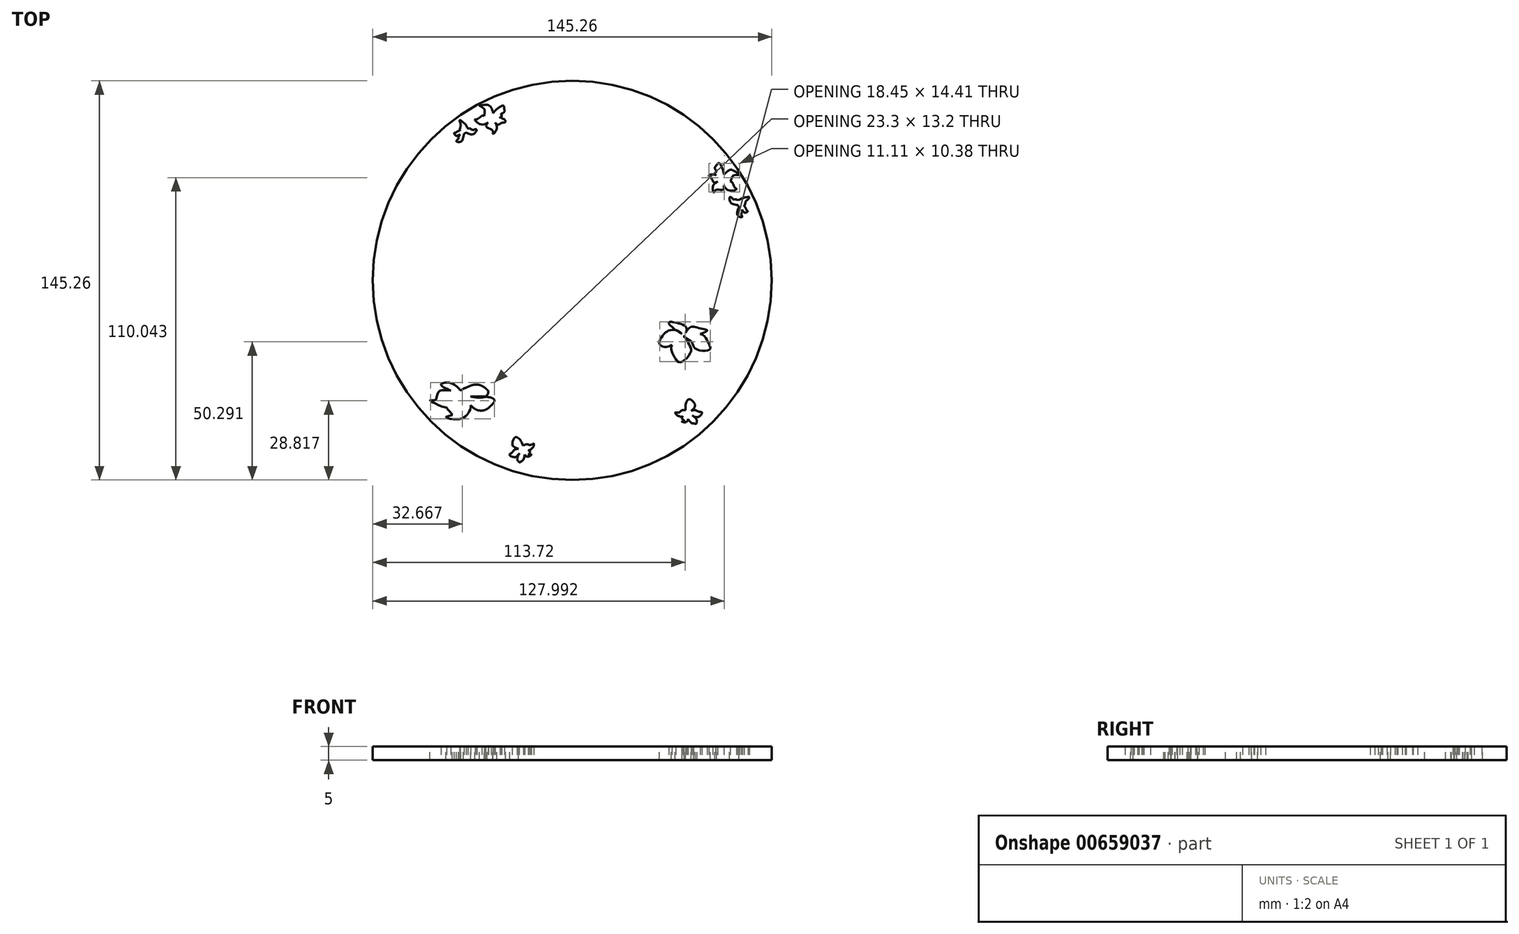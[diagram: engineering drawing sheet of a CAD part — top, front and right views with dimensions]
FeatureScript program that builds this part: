
annotation { "Feature Type Name" : "Feature", "Feature Type Description" : "" }
export const myFeature = defineFeature(function(context is Context, id is Id, definition is map)
    precondition{}
    {
        {
            var Q0;
            Q0=qCreatedBy(makeId("Top.planeOp"),FACE);
            var sketch = newSketch(context, id + "F0", { "sketchPlane" : qUnion([Q0])});
            skCircle(sketch, "E0", {"center": v(0, 0) * mm, "radius": 74.63 * mm});
            skFitSpline(sketch, "E1", {"points": [v(-40.91, 58.34) * mm, v(-40.6, 56.7) * mm, v(-40.85, 55.34) * mm, v(-40.76, 53.16) * mm, v(-39.4, 53.35) * mm, v(-38.04, 55.3) * mm, v(-40.91, 58.34) * mm]});
            skFitSpline(sketch, "E2", {"points": [v(-38.04, 55.3) * mm, v(-37.18, 55.3) * mm, v(-36.22, 54.76) * mm, v(-35.4, 55.04) * mm, v(-34.76, 54.83) * mm, v(-35.4, 53.73) * mm, v(-36.63, 53.12) * mm, v(-38.68, 53.8) * mm], "startDerivative": vector(6.82, 1.47) * mm, "endDerivative": vector(-10.95, 4.9) * mm});
            skFitSpline(sketch, "E3", {"points": [v(-40.98, 54.45) * mm, v(-41.87, 54.19) * mm, v(-42.51, 53.68) * mm, v(-42.97, 53.73) * mm, v(-42.43, 52.71) * mm, v(-40.76, 53.16) * mm], "startDerivative": vector(-4.99, 0.27) * mm, "endDerivative": vector(6.89, 3.52) * mm});
            skFitSpline(sketch, "E4", {"points": [v(-40.76, 53.16) * mm, v(-41.37, 52.23) * mm, v(-41.37, 51.64) * mm, v(-42, 51.05) * mm, v(-42.16, 50.65) * mm, v(-41.37, 50.38) * mm, v(-40.18, 50.75) * mm, v(-39.4, 53.35) * mm], "startDerivative": vector(-5.91, -5.6) * mm, "endDerivative": vector(2.42, 13) * mm});
            skFitSpline(sketch, "E5", {"points": [v(-39.6, 52.34) * mm, v(-39.4, 51.05) * mm, v(-38.76, 50.73) * mm, v(-38.22, 50) * mm, v(-38.49, 49.87) * mm, v(-38.09, 49.74) * mm, v(-37.4, 50.51) * mm, v(-37.36, 51.43) * mm, v(-37.42, 52.34) * mm, v(-37.96, 53.48) * mm], "startDerivative": vector(-0.1, -10.73) * mm, "endDerivative": vector(-5.2, 8.29) * mm});
            skFitSpline(sketch, "E6", {"points": [v(-33.8, 63.65) * mm, v(-31.96, 62.26) * mm, v(-32, 59.88) * mm, v(-30.3, 58.89) * mm, v(-28.92, 60.06) * mm, v(-29.1, 62.04) * mm, v(-30.24, 63.73) * mm, v(-32.5, 63.84) * mm, v(-33.8, 63.65) * mm]});
            skFitSpline(sketch, "E7", {"points": [v(-28.82, 60.86) * mm, v(-27.82, 61.97) * mm, v(-25.8, 63.47) * mm, v(-25.07, 63.62) * mm, v(-24.81, 62.92) * mm, v(-24.81, 61.2) * mm, v(-25.91, 60.54) * mm, v(-25.62, 59.77) * mm, v(-27.41, 59.13) * mm, v(-28.92, 60.06) * mm], "startDerivative": vector(7.39, 9) * mm, "endDerivative": vector(-9.5, 11.77) * mm});
            skFitSpline(sketch, "E8", {"points": [v(-32, 59.88) * mm, v(-32.91, 59.88) * mm, v(-34.76, 58.63) * mm, v(-35.4, 58.6) * mm, v(-33.94, 57.02) * mm, v(-30.68, 57.48) * mm, v(-29.61, 59.13) * mm, v(-29.64, 59.13) * mm], "startDerivative": vector(-7.49, 2.17) * mm, "endDerivative": vector(-5.62, -1.67) * mm});
            skFitSpline(sketch, "E9", {"points": [v(-30.68, 57.48) * mm, v(-31.26, 55.98) * mm, v(-28.92, 54.45) * mm, v(-28.92, 53.48) * mm, v(-28.3, 53.73) * mm, v(-27.41, 56.01) * mm, v(-29.61, 59.13) * mm], "startDerivative": vector(-8.57, -10.2) * mm, "endDerivative": vector(-13.08, 12.83) * mm});
            skFitSpline(sketch, "E10", {"points": [v(-28.08, 57.48) * mm, v(-27.05, 56.65) * mm, v(-25.4, 57.48) * mm, v(-24.6, 57.48) * mm, v(-24.26, 58.12) * mm, v(-26.22, 59.3) * mm, v(-26.33, 59.26) * mm], "startDerivative": vector(4.67, -5.14) * mm, "endDerivative": vector(-1.23, -1.34) * mm});
            skFitSpline(sketch, "E11", {"points": [v(40.7, -20.4) * mm, v(36.32, -23.45) * mm, v(36.83, -27.11) * mm, v(39.27, -29.76) * mm, v(43.24, -25.8) * mm, v(42.42, -23.05) * mm, v(40.7, -20.4) * mm]});
            skFitSpline(sketch, "E12", {"points": [v(40.7, -20.4) * mm, v(43.34, -22.23) * mm, v(44.76, -24.78) * mm, v(50.05, -25.18) * mm, v(49.64, -22.74) * mm, v(46.6, -19.49) * mm, v(40.7, -20.4) * mm]});
            skFitSpline(sketch, "E13", {"points": [v(40.7, -20.4) * mm, v(38.11, -18.16) * mm, v(34.68, -18.49) * mm, v(32.72, -20.4) * mm, v(31.82, -23.06) * mm, v(34.02, -24.2) * mm, v(36.32, -23.45) * mm], "startDerivative": vector(-12.48, 15.48) * mm, "endDerivative": vector(13.93, 7.55) * mm});
            skFitSpline(sketch, "E14", {"points": [v(39.94, -19.46) * mm, v(36.32, -16.93) * mm, v(35.17, -15.3) * mm, v(38.11, -15.46) * mm, v(41.62, -17.26) * mm, v(40.7, -20.4) * mm], "startDerivative": vector(-16.5, 10.24) * mm, "endDerivative": vector(-8.67, -17.52) * mm});
            skFitSpline(sketch, "E15", {"points": [v(41.27, -19.23) * mm, v(43.18, -16.93) * mm, v(46.7, -17.5) * mm, v(49.14, -18.16) * mm, v(46.6, -19.49) * mm], "startDerivative": vector(6.21, 12.18) * mm, "endDerivative": vector(-15.88, -6.24) * mm});
            skFitSpline(sketch, "E16", {"points": [v(-40.74, -40.65) * mm, v(-44.04, -42.43) * mm, v(-45.7, -46.36) * mm, v(-43.79, -48.9) * mm, v(-45.95, -49.66) * mm, v(-42.01, -50.55) * mm, v(-38.08, -48.65) * mm, v(-36.9, -45.47) * mm, v(-37.95, -42.3) * mm, v(-40.74, -40.65) * mm]});
            skFitSpline(sketch, "E17", {"points": [v(-36.9, -45.47) * mm, v(-32.84, -47.38) * mm, v(-29.41, -45.47) * mm, v(-28.4, -43.44) * mm, v(-31.7, -42.3) * mm, v(-36.9, -42.3) * mm], "startDerivative": vector(18.8, -13.39) * mm, "endDerivative": vector(-21.47, 0.17) * mm});
            skFitSpline(sketch, "E18", {"points": [v(-40.74, -40.65) * mm, v(-48.74, -40.65) * mm, v(-49.88, -43.57) * mm, v(-51.78, -43.57) * mm, v(-48.48, -45.47) * mm, v(-45.7, -46.36) * mm], "startDerivative": vector(-35.6, 5.67) * mm, "endDerivative": vector(13.06, -2.8) * mm});
            skFitSpline(sketch, "E19", {"points": [v(-44.22, -40.1) * mm, v(-47.72, -37.86) * mm, v(-44.22, -37.35) * mm, v(-40.74, -40.1) * mm, v(-40.74, -40.65) * mm], "startDerivative": vector(-18.42, 7.74) * mm, "endDerivative": vector(-1.16, -4.68) * mm});
            skFitSpline(sketch, "E20", {"points": [v(-40.7, -40.48) * mm, v(-34.68, -37.9) * mm, v(-31.45, -39.36) * mm, v(-30.56, -40.65) * mm, v(-35.22, -42.32) * mm], "startDerivative": vector(19.8, 12.05) * mm, "endDerivative": vector(-23.97, -4.7) * mm});
            skFitSpline(sketch, "E21", {"points": [v(42.46, -43.24) * mm, v(41.27, -45.47) * mm, v(41.27, -47.24) * mm, v(41.27, -48.54) * mm, v(44.44, -46.36) * mm, v(44.39, -44.5) * mm, v(42.46, -43.24) * mm]});
            skFitSpline(sketch, "E22", {"points": [v(41.27, -47.24) * mm, v(39.94, -47.24) * mm, v(39.3, -47.81) * mm, v(38.11, -48.15) * mm, v(37.52, -48.1) * mm, v(38.11, -49.07) * mm, v(39.07, -49.47) * mm, v(39.94, -49.58) * mm, v(41.27, -48.54) * mm], "startDerivative": vector(-11.28, 1.59) * mm, "endDerivative": vector(9.13, 8.93) * mm});
            skFitSpline(sketch, "E23", {"points": [v(40.35, -49.38) * mm, v(39.94, -50.13) * mm, v(40.18, -50.52) * mm, v(40.8, -51.05) * mm, v(40.27, -51.26) * mm, v(39.94, -51.4) * mm, v(40.8, -51.63) * mm, v(41.57, -51.48) * mm, v(42.05, -50.96) * mm, v(42.15, -50.35) * mm, v(42.16, -49.77) * mm, v(42.1, -49.3) * mm, v(41.85, -49) * mm, v(41.27, -48.54) * mm], "startDerivative": vector(-6.6, -9.03) * mm, "endDerivative": vector(-6.76, 6.2) * mm});
            skFitSpline(sketch, "E24", {"points": [v(42.15, -50.35) * mm, v(42.66, -51.1) * mm, v(43.68, -52.02) * mm, v(44.58, -52.1) * mm, v(45.02, -52.24) * mm, v(45.24, -51.81) * mm, v(45.4, -50.92) * mm, v(44.83, -50) * mm, v(43.81, -49.2) * mm, v(42.65, -49) * mm, v(41.46, -48.71) * mm], "startDerivative": vector(4.58, -7.2) * mm, "endDerivative": vector(-10.04, 3.34) * mm});
            skFitSpline(sketch, "E25", {"points": [v(43.32, -47.5) * mm, v(45, -47.24) * mm, v(45.9, -47.71) * mm, v(46.82, -47.86) * mm, v(47.23, -48.15) * mm, v(46.99, -48.85) * mm, v(46.37, -49.4) * mm, v(45.56, -49.76) * mm, v(44.22, -49.43) * mm, v(43.81, -49.2) * mm], "startDerivative": vector(12.1, 3.78) * mm, "endDerivative": vector(-3.9, 2.83) * mm});
            skCircle(sketch, "E26.0", {"center": v(0, 0) * mm, "radius": 72.63 * mm});
            skFitSpline(sketch, "E27.MirrorCS", {"points": [v(61.79, 25.88) * mm, v(61.85, 24.77) * mm, v(61.56, 24.26) * mm, v(61.82, 23.43) * mm, v(61.76, 23) * mm, v(60.93, 23.16) * mm, v(60.09, 24.08) * mm, v(60.7, 26.71) * mm], "startDerivative": vector(2.34, -7.8) * mm, "endDerivative": vector(4.22, 11.8) * mm});
            skFitSpline(sketch, "E28.MirrorCS", {"points": [v(62.62, 26.88) * mm, v(63.26, 26.22) * mm, v(63.57, 25.46) * mm, v(63.99, 25.28) * mm, v(63.02, 24.66) * mm, v(61.79, 25.88) * mm], "startDerivative": vector(4.46, -2.24) * mm, "endDerivative": vector(-4.23, 6.47) * mm});
            skFitSpline(sketch, "E29.MirrorCS", {"points": [v(60.38, 25.8) * mm, v(59.56, 24.72) * mm, v(58.84, 24.76) * mm, v(58.02, 24.4) * mm, v(58.18, 24.15) * mm, v(57.77, 24.23) * mm, v(57.55, 25.26) * mm, v(57.98, 26.06) * mm, v(58.48, 26.83) * mm, v(59.55, 27.55) * mm], "startDerivative": vector(-5.25, -9.36) * mm, "endDerivative": vector(8.63, 4.6) * mm});
            skFitSpline(sketch, "E30.MirrorCS", {"points": [v(52.93, 35.92) * mm, v(51.62, 35.72) * mm, v(50.6, 37.26) * mm, v(49.9, 37.66) * mm, v(49.93, 38.38) * mm, v(52.21, 38.43) * mm, v(52.3, 38.34) * mm], "startDerivative": vector(-6.6, -2.14) * mm, "endDerivative": vector(0.8, -0.88) * mm});
            skFitSpline(sketch, "E31.MirrorC", {"points": [v(64.5, 30.3) * mm, v(63.42, 29.03) * mm, v(62.95, 27.73) * mm, v(61.79, 25.88) * mm, v(60.7, 26.71) * mm, v(60.5, 29.08) * mm, v(64.5, 30.3) * mm]});
            skFitSpline(sketch, "E32.MirrorCS", {"points": [v(60.5, 29.08) * mm, v(59.74, 29.5) * mm, v(58.64, 29.53) * mm, v(58.06, 30.17) * mm, v(57.41, 30.3) * mm, v(57.42, 29.04) * mm, v(58.18, 27.9) * mm, v(60.3, 27.47) * mm], "startDerivative": vector(-5.19, 4.66) * mm, "endDerivative": vector(11.46, -1.13) * mm});
            skFitSpline(sketch, "E33.MirrorCS", {"points": [v(55.26, 38.5) * mm, v(54.93, 39.95) * mm, v(53.93, 42.26) * mm, v(53.37, 42.75) * mm, v(52.8, 42.27) * mm, v(51.94, 40.78) * mm, v(52.57, 39.66) * mm, v(51.93, 39.14) * mm, v(53.17, 37.69) * mm, v(54.94, 37.75) * mm], "startDerivative": vector(-1.94, 11.48) * mm, "endDerivative": vector(14.08, 5.5) * mm});
            skFitSpline(sketch, "E34.MirrorCS", {"points": [v(57.52, 36.06) * mm, v(58.31, 35.6) * mm, v(59.3, 33.6) * mm, v(59.83, 33.26) * mm, v(57.78, 32.62) * mm, v(55.18, 34.64) * mm, v(55.08, 36.6) * mm, v(55.1, 36.58) * mm], "startDerivative": vector(7.58, -1.84) * mm, "endDerivative": vector(4.05, -4.25) * mm});
            skFitSpline(sketch, "E35.MirrorCS", {"points": [v(55.18, 34.64) * mm, v(54.94, 33.04) * mm, v(52.15, 32.88) * mm, v(51.66, 32.02) * mm, v(51.25, 32.57) * mm, v(51.62, 34.99) * mm, v(55.08, 36.6) * mm], "startDerivative": vector(2.36, -13.1) * mm, "endDerivative": vector(17.72, 4.63) * mm});
            skFitSpline(sketch, "E36.MirrorC", {"points": [v(60.95, 38.45) * mm, v(58.67, 38.15) * mm, v(57.52, 36.06) * mm, v(55.56, 36.04) * mm, v(54.94, 37.75) * mm, v(56.08, 39.38) * mm, v(57.9, 40.28) * mm, v(59.93, 39.24) * mm, v(60.95, 38.45) * mm]});
            skFitSpline(sketch, "E37.MirrorCS", {"points": [v(-16.04, -61.73) * mm, v(-15.35, -62.22) * mm, v(-15.4, -62.68) * mm, v(-15.8, -63.45) * mm, v(-15.18, -63.4) * mm, v(-14.82, -63.39) * mm, v(-15.55, -63.97) * mm, v(-16.27, -64.14) * mm, v(-16.93, -63.87) * mm, v(-17.27, -63.35) * mm, v(-17.52, -62.83) * mm, v(-17.67, -62.4) * mm, v(-17.56, -62) * mm, v(-17.28, -61.36) * mm], "startDerivative": vector(9.76, -5.45) * mm, "endDerivative": vector(3.55, 8.47) * mm});
            skFitSpline(sketch, "E38.MirrorCS", {"points": [v(-17.82, -60.18) * mm, v(-16.56, -59.6) * mm, v(-15.74, -59.85) * mm, v(-14.52, -59.67) * mm, v(-14, -59.37) * mm, v(-14.13, -60.5) * mm, v(-14.83, -61.26) * mm, v(-15.58, -61.73) * mm, v(-17.28, -61.36) * mm], "startDerivative": vector(9.58, 6.15) * mm, "endDerivative": vector(-12.03, 4.3) * mm});
            skFitSpline(sketch, "E39.MirrorCS", {"points": [v(-17.27, -63.35) * mm, v(-17.42, -64.26) * mm, v(-17.97, -65.5) * mm, v(-18.75, -65.95) * mm, v(-19.09, -66.27) * mm, v(-19.47, -65.97) * mm, v(-20, -65.23) * mm, v(-19.86, -64.15) * mm, v(-19.26, -63) * mm, v(-18.28, -62.34) * mm, v(-17.38, -61.6) * mm], "startDerivative": vector(-1.16, -8.45) * mm, "endDerivative": vector(7.72, 7.23) * mm});
            skFitSpline(sketch, "E40.MirrorCS", {"points": [v(-19.53, -61.26) * mm, v(-21.16, -61.72) * mm, v(-21.77, -62.52) * mm, v(-22.55, -63.04) * mm, v(-22.8, -63.48) * mm, v(-22.3, -64) * mm, v(-21.5, -64.26) * mm, v(-20.61, -64.24) * mm, v(-19.54, -63.38) * mm, v(-19.26, -63) * mm], "startDerivative": vector(-12.57, -1.61) * mm, "endDerivative": vector(2.36, 4.2) * mm});
            skFitSpline(sketch, "E41.MirrorC", {"points": [v(-20.52, -57.02) * mm, v(-18.56, -58.58) * mm, v(-17.82, -60.18) * mm, v(-17.28, -61.36) * mm, v(-21.02, -60.69) * mm, v(-21.75, -58.96) * mm, v(-20.52, -57.02) * mm]});
            skLineSegment(sketch, "E42", {"start": v(-35.22, -42.32) * mm, "end": v(-35.42, -42.28) * mm});
            skFitSpline(sketch, "E43", {"points": [v(-40.74, -40.1) * mm, v(-39.72, -39.47) * mm, v(-37.69, -38.62) * mm, v(-34.68, -37.9) * mm, v(-31.45, -39.36) * mm, v(-30.56, -40.65) * mm, v(-31.7, -42.3) * mm, v(-36.9, -42.3) * mm], "startDerivative": vector(9.53, 6.46) * mm, "endDerivative": vector(-29.55, 4.4) * mm});
            skFitSpline(sketch, "E44", {"points": [v(-36.9, -42.3) * mm, v(-34.89, -42.6) * mm, v(-32.2, -43.04) * mm, v(-28.4, -43.44) * mm, v(-29.41, -45.47) * mm, v(-32.84, -47.38) * mm, v(-35.54, -46.7) * mm, v(-36.9, -45.47) * mm], "startDerivative": vector(16.39, -1.98) * mm, "endDerivative": vector(-10.05, 11.08) * mm});
            skSolve(sketch);
        }
        {
            var Q0;
            Q0=makeQuery(id+"F0.imprint","IMPRINT",FACE,{"disambiguationData":[TD([[makeQuery(id+"F0.imprint","IMPRINT",EDGE,{"derivedFrom":sQuery(id+"F0.wireOp",EDGE,"E26.0")}),1.0]])]});
            var Q1;
            {var subQ6=sQuery(id+"F0.wireOp",EDGE,"E3");Q1=makeQuery(id+"F0.imprint","IMPRINT",FACE,{"disambiguationData":[TD([[makeQuery(id+"F0.imprint","IMPRINT",EDGE,{"derivedFrom":subQ6}),-1.0]])]});}
            var Q2;
            {var subQ0=sQuery(id+"F0.wireOp",EDGE,"E33.MirrorCS");var subQ1=sQuery(id+"F0.wireOp",EDGE,"E30.MirrorCS");var subQ2=makeQuery(id+"F0.imprint","INTERSECT",VERTEX,{"disambiguationData":[OD(0.0)],"derivedFrom":[subQ1,subQ0]});Q2=makeQuery(id+"F0.imprint","IMPRINT",FACE,{"disambiguationData":[TD([[makeQuery(id+"F0.imprint","IMPRINT",EDGE,{"disambiguationData":[TD([[subQ2,1.0]])],"derivedFrom":subQ1}),-1.0]])]});}
            var Q3;
            {var subQ0=sQuery(id+"F0.wireOp",EDGE,"E14");var subQ1=sQuery(id+"F0.wireOp",EDGE,"E13");var subQ2=makeQuery(id+"F0.imprint","INTERSECT",VERTEX,{"disambiguationData":[OD(0.0)],"derivedFrom":[subQ1,subQ0]});Q3=makeQuery(id+"F0.imprint","IMPRINT",FACE,{"disambiguationData":[TD([[makeQuery(id+"F0.imprint","IMPRINT",EDGE,{"disambiguationData":[TD([[subQ2,-1.0]])],"derivedFrom":subQ1}),1.0]])]});}
            var Q4;
            {var subQ0=sQuery(id+"F0.wireOp",EDGE,"E10");var subQ1=sQuery(id+"F0.wireOp",EDGE,"E7");var subQ2=makeQuery(id+"F0.imprint","INTERSECT",VERTEX,{"disambiguationData":[OD(0.0)],"derivedFrom":[subQ1,subQ0]});Q4=makeQuery(id+"F0.imprint","IMPRINT",FACE,{"disambiguationData":[TD([[makeQuery(id+"F0.imprint","IMPRINT",EDGE,{"disambiguationData":[TD([[subQ2,1.0]])],"derivedFrom":subQ1}),-1.0]])]});}
            var Q5;
            {var subQ0=sQuery(id+"F0.wireOp",EDGE,"E40.MirrorCS");var subQ1=sQuery(id+"F0.wireOp",EDGE,"E39.MirrorCS");var subQ2=makeQuery(id+"F0.imprint","INTERSECT",VERTEX,{"disambiguationData":[OD(0.0)],"derivedFrom":[subQ1,subQ0]});Q5=makeQuery(id+"F0.imprint","IMPRINT",FACE,{"disambiguationData":[TD([[makeQuery(id+"F0.imprint","IMPRINT",EDGE,{"disambiguationData":[TD([[subQ2,1.0]])],"derivedFrom":subQ1}),-1.0]])]});}
            var Q6;
            {var subQ0=sQuery(id+"F0.wireOp",EDGE,"E25");var subQ1=sQuery(id+"F0.wireOp",EDGE,"E24");var subQ2=makeQuery(id+"F0.imprint","INTERSECT",VERTEX,{"disambiguationData":[OD(0.0)],"derivedFrom":[subQ1,subQ0]});Q6=makeQuery(id+"F0.imprint","IMPRINT",FACE,{"disambiguationData":[TD([[makeQuery(id+"F0.imprint","IMPRINT",EDGE,{"disambiguationData":[TD([[subQ2,1.0]])],"derivedFrom":subQ1}),1.0]])]});}
            var Q7;
            {var subQ0=sQuery(id+"F0.wireOp",EDGE,"E12");var subQ1=sQuery(id+"F0.wireOp",EDGE,"E11");var subQ3=makeQuery(id+"F0.imprint","INTERSECT",VERTEX,{"derivedFrom":[subQ1,subQ0]});Q7=makeQuery(id+"F0.imprint","IMPRINT",FACE,{"disambiguationData":[TD([[makeQuery(id+"F0.imprint","IMPRINT",EDGE,{"disambiguationData":[TD([[subQ3,-1.0]])],"derivedFrom":subQ1}),1.0]])]});}
            var Q8;
            {var subQ0=sQuery(id+"F0.wireOp",EDGE,"E14");var subQ1=sQuery(id+"F0.wireOp",EDGE,"E12");var subQ3=makeQuery(id+"F0.imprint","INTERSECT",VERTEX,{"derivedFrom":[subQ1,subQ0]});Q8=makeQuery(id+"F0.imprint","IMPRINT",FACE,{"disambiguationData":[TD([[makeQuery(id+"F0.imprint","IMPRINT",EDGE,{"disambiguationData":[TD([[subQ3,-1.0]])],"derivedFrom":subQ1}),1.0]])]});}
            var Q9;
            {var subQ0=sQuery(id+"F0.wireOp",EDGE,"E44");var subQ1=sQuery(id+"F0.wireOp",EDGE,"E43");var subQ2=makeQuery(id+"F0.imprint","INTERSECT",VERTEX,{"disambiguationData":[OD(0.0)],"derivedFrom":[subQ1,subQ0]});Q9=makeQuery(id+"F0.imprint","IMPRINT",FACE,{"disambiguationData":[TD([[makeQuery(id+"F0.imprint","IMPRINT",EDGE,{"disambiguationData":[TD([[subQ2,1.0]])],"derivedFrom":subQ1}),-1.0]])]});}
            extrude(context, id + "F1", {"entities" : qUnion([Q0, Q1, Q2, Q3, Q4, Q5, Q6, Q7, Q8, Q9]), "depth" : 5 * mm, "offsetDistance" : 25 * mm});
        }
    });
